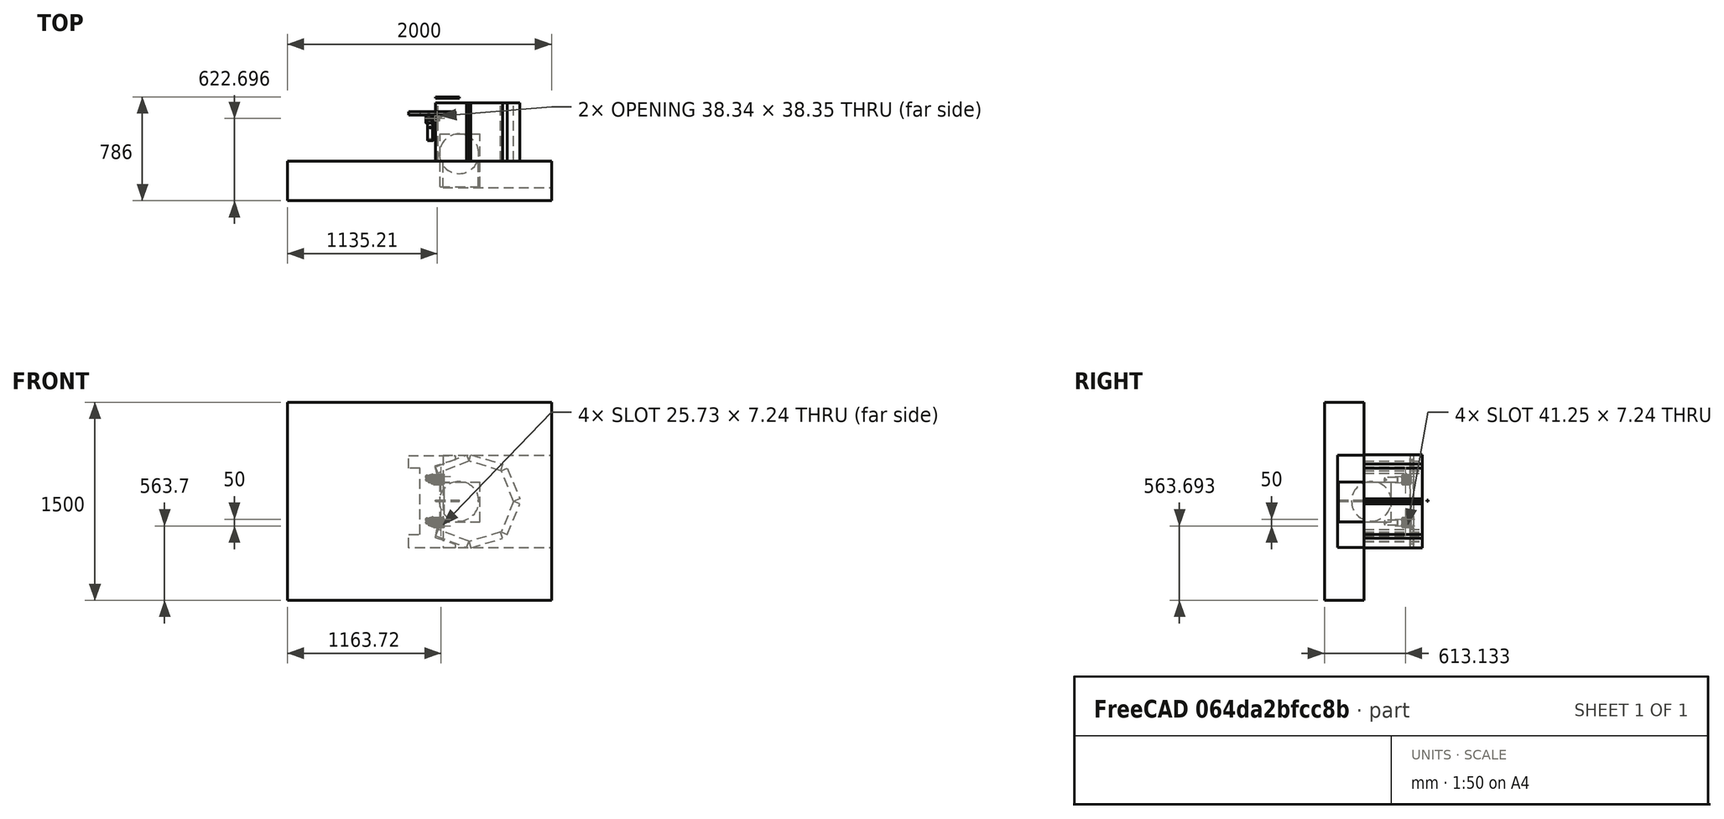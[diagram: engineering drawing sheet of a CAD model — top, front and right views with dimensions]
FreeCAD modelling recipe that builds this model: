
FCSTD DOCUMENT  (FreeCAD 0.17R13541 (Git))
Label: modification4
License: All rights reserved
LicenseURL: http://en.wikipedia.org/wiki/All_rights_reserved
objects: Mesh::Feature×7, Part::Feature×6, Part::Extrusion×6, Part::Box×4, Sketcher::SketchObject×3, Part::Part2DObjectPython×3, Part::Mirroring×3, PartDesign::Pad×2, App::MeasureDistance×2, PartDesign::Body×2, Part::Sphere×1, Part::Cut×1, App::DocumentObjectGroup×1
note: 33 computed .brp shape members not serialized (recipe doc carries the construction recipe); baked Part::Feature solids carry a one-line shape summary decoded from their .brp

FEATURE [Mesh::Feature] main_part  label="main part"
  Placement = pos=(-233.65,190,-253.8) rot=(0,0,1;0rad)
FEATURE [Sketcher::SketchObject] Sketch
  MapMode = 5
  Placement = pos=(0,0,0) rot=(1,0,0;1.5708rad)
  Support = -> [XZ_Plane]
  sketch-geometry (5):
    g0: LineSegment StartX=-1300 StartY=750 StartZ=0 EndX=700 EndY=750 EndZ=0
    g1: LineSegment StartX=700 StartY=750 StartZ=0 EndX=700 EndY=-750 EndZ=0
    g2: LineSegment StartX=700 StartY=-750 StartZ=0 EndX=-1300 EndY=-750 EndZ=0
    g3: LineSegment StartX=-1300 StartY=-750 StartZ=0 EndX=-1300 EndY=750 EndZ=0
    g4: LineSegment [constr] StartX=0 StartY=0 StartZ=0 EndX=700 EndY=0 EndZ=0
  constraints (15):
    c: Coincident(g0,g1)
    c: Coincident(g1,g2)
    c: Coincident(g2,g3)
    c: Coincident(g3,g0)
    c: Horizontal(g0)
    c: Horizontal(g2)
    c: Vertical(g1)
    c: Vertical(g3)
    c: Symmetric(g0,g1,g-1)
    c: DistanceY(g1,g1) = 1500
    c: Distance(g0) = 2000
    c: PointOnObject(g4,g1)
    c: Horizontal(g4)
    c: Coincident(g4,g-1)
    c: DistanceX(g4,g4) = 700
FEATURE [PartDesign::Pad] Pad
  Length = 300
  Length2 = 100
  Placement = pos=(0,0,0) rot=(1,0,0;1.5708rad)
  Profile = -> Sketch
  Type = 0
FEATURE [App::MeasureDistance] Distance  label="Distance: 602.90 mm"
  Distance = 602.898
  P1 = (101.677,440,301.449)
  P2 = (101.677,440,-301.449)
FEATURE [Mesh::Feature] _legs  label="4legs"
  Placement = pos=(-233.65,190,-253.8) rot=(0,0,1;0rad)
FEATURE [Mesh::Feature] _supports  label="4supports"
  Placement = pos=(-233.65,190,-253.8) rot=(0,0,1;0rad)
FEATURE [Mesh::Feature] frame
  Placement = pos=(-233.65,190,-253.8) rot=(0,0,1;0rad)
FEATURE [Mesh::Feature] scanhead
  Placement = pos=(-233.65,190,-253.8) rot=(0,0,1;0rad)
FEATURE [Mesh::Feature] NDD
  Placement = pos=(-233.65,190,-253.8) rot=(0,0,1;0rad)
FEATURE [Mesh::Feature] baseplate
  Placement = pos=(-233.65,190,-253.8) rot=(0,0,1;0rad)
FEATURE [Sketcher::SketchObject] Sketch002
  AttachmentOffset = pos=(0,0,-375) rot=(0,0,1;0rad)
  MapMode = 5
  Placement = pos=(0,375,3.9e-11) rot=(1,0,0;1.5708rad)
  Support = -> [XZ_Plane001]
  sketch-geometry (16):
    g0: LineSegment StartX=-381.934 StartY=346.795 StartZ=0 EndX=-29.0273 EndY=346.795 EndZ=0
    g1: LineSegment StartX=-29.0273 StartY=346.795 StartZ=0 EndX=-29.0273 EndY=314.886 EndZ=0
    g2: LineSegment StartX=-29.0273 StartY=314.886 StartZ=0 EndX=-185.502 EndY=264.81 EndZ=0
    g3: LineSegment StartX=-185.502 StartY=264.81 StartZ=0 EndX=-168.803 EndY=207.974 EndZ=0
    g4: LineSegment StartX=-168.803 StartY=207.974 StartZ=0 EndX=-114.949 EndY=205.162 EndZ=0
    g5: LineSegment StartX=-114.949 StartY=205.162 StartZ=0 EndX=-114.949 EndY=-201.338 EndZ=0
    g6: LineSegment StartX=-114.949 StartY=-201.338 StartZ=0 EndX=-167.27 EndY=-205.799 EndZ=0
    g7: LineSegment StartX=-167.27 StartY=-205.799 StartZ=0 EndX=-182.648 EndY=-273.392 EndZ=0
    g8: LineSegment StartX=-182.648 StartY=-273.392 StartZ=0 EndX=-29.0215 EndY=-323.099 EndZ=0
    g9: LineSegment StartX=-29.0215 StartY=-323.099 StartZ=0 EndX=-29.0215 EndY=-352.213 EndZ=0
    g10: LineSegment StartX=-29.0215 StartY=-352.213 StartZ=0 EndX=-381.23 EndY=-352.213 EndZ=0
    g11: LineSegment StartX=-381.23 StartY=-352.213 StartZ=0 EndX=-381.23 EndY=-251.379 EndZ=0
    g12: LineSegment StartX=-381.23 StartY=-251.379 StartZ=0 EndX=-296.018 EndY=-251.379 EndZ=0
    g13: LineSegment StartX=-296.018 StartY=-251.379 StartZ=0 EndX=-296.018 EndY=249.512 EndZ=0
    g14: LineSegment StartX=-296.018 StartY=249.512 StartZ=0 EndX=-381.934 EndY=249.512 EndZ=0
    g15: LineSegment StartX=-381.934 StartY=249.512 StartZ=0 EndX=-381.934 EndY=346.795 EndZ=0
  constraints (26):
    c: Horizontal(g0)
    c: Coincident(g0,g1)
    c: Vertical(g1)
    c: Coincident(g1,g2)
    c: Coincident(g2,g3)
    c: Coincident(g3,g4)
    c: Coincident(g4,g5)
    c: Vertical(g5)
    c: Coincident(g5,g6)
    c: Coincident(g6,g7)
    c: Coincident(g7,g8)
    c: Coincident(g8,g9)
    c: Vertical(g9)
    c: Coincident(g9,g10)
    c: Horizontal(g10)
    c: Coincident(g10,g11)
    c: Vertical(g11)
    c: Coincident(g11,g12)
    c: Horizontal(g12)
    c: Coincident(g12,g13)
    c: Vertical(g13)
    c: Coincident(g13,g14)
    c: Horizontal(g14)
    c: Coincident(g14,g15)
    c: Vertical(g15)
    c: Coincident(g15,g0)
FEATURE [PartDesign::Pad] Pad002
  Length = 25
  Length2 = 100
  Placement = pos=(0,0,0) rot=(1,0,0;1.5708rad)
  Profile = -> Sketch002
  Type = 0
FEATURE [PartDesign::Body] Body001
  Group = -> [Sketch002,Pad002]
  Origin = -> Origin001
  Tip = -> Pad002
FEATURE [Part::Box] Box  label="Cube"
  AttacherType = Attacher::AttachEngine3D
  Height = 10
  Length = 180
  Placement = pos=(-178,476,0) rot=(0,0,1;0rad)
  Width = 10
FEATURE [Part::Sphere] Sphere
  Angle1 = -90
  Angle2 = 90
  Angle3 = 360
  AttacherType = Attacher::AttachEngine3D
  Placement = pos=(0,55,0) rot=(0,0,1;0rad)
  Radius = 150
FEATURE [Part::Box] Box001  label="Cube001"
  AttacherType = Attacher::AttachEngine3D
  Height = 302
  Length = 302
  Placement = pos=(-144,-194,-156) rot=(0,0,1;0rad)
  Width = 400
FEATURE [Part::Feature] Part__Feature002  label="LPH250-E0W001"
  Placement = pos=(36,41,233) rot=(1,0,0;1.5708rad)
  shape: bbox 76.2 x 274.8 x 98.13 mm, 1972 faces, 0 solids (baked)
FEATURE [Part::Feature] Part__Feature003  label="0701-E0W001"
  Placement = pos=(-219,255,162) rot=(0,0,1;0rad)
  shape: bbox 37.74 x 200 x 37.74 mm, 44 faces (baked)
FEATURE [Part::Feature] Part__Feature006  label="TTN038315-E0W"
  Placement = pos=(-243,310,110) rot=(0,1,0;1.5708rad)
  shape: bbox 136.2 x 63.5 x 82.81 mm, 771 faces, 12 solids (baked)
FEATURE [Part::Feature] Part__Feature007  label="TTN038315-E0W001"
  Placement = pos=(-243,310,-214) rot=(0,1,0;1.5708rad)
  shape: bbox 136.2 x 63.5 x 82.81 mm, 771 faces, 12 solids (baked)
FEATURE [Part::Feature] Part__Feature008  label="LPH250-E0W002"
  Placement = pos=(36,41,-89) rot=(1,0,0;1.5708rad)
  shape: bbox 76.2 x 274.8 x 98.13 mm, 1972 faces, 0 solids (baked)
FEATURE [Part::Feature] Part__Feature009  label="0701-E0W002"
  Placement = pos=(-219,255,-163) rot=(0,0,1;0rad)
  shape: bbox 37.74 x 200 x 37.74 mm, 44 faces (baked)
FEATURE [Part::Box] Box002  label="Cube002"
  AttacherType = Attacher::AttachEngine3D
  Height = 10
  Length = 10
  Placement = pos=(145,-197,0) rot=(0,0,1;0rad)
  Width = 200
FEATURE [Sketcher::SketchObject] Sketch001
  AttachmentOffset = pos=(-20,0,0) rot=(0,0,1;0rad)
  MapMode = 5
  Placement = pos=(-20,0,0) rot=(-1,0,0;1.5708rad)
  Support = -> [Pad]
  sketch-geometry (24):
    g0: LineSegment StartX=-153.123 StartY=262.289 StartZ=0 EndX=81.8002 EndY=347.794 EndZ=0
    g1: LineSegment StartX=81.8002 StartY=347.794 StartZ=0 EndX=98.9012 EndY=300.809 EndZ=0
    g2: LineSegment StartX=98.9012 StartY=300.809 StartZ=0 EndX=-136.022 EndY=215.304 EndZ=0
    g3: LineSegment StartX=-136.022 StartY=215.304 StartZ=0 EndX=-153.123 EndY=262.289 EndZ=0
    g4: LineSegment StartX=118.778 StartY=348.433 StartZ=0 EndX=353.701 EndY=262.928 EndZ=0
    g5: LineSegment StartX=101.677 StartY=301.449 StartZ=0 EndX=118.778 EndY=348.433 EndZ=0
    g6: LineSegment StartX=336.6 StartY=215.944 StartZ=0 EndX=101.677 EndY=301.449 EndZ=0
    g7: LineSegment StartX=353.701 StartY=262.928 StartZ=0 EndX=336.6 EndY=215.944 EndZ=0
    g8: LineSegment StartX=463.416 StartY=0.832942 StartZ=0 EndX=338.416 EndY=217.339 EndZ=0
    g9: LineSegment StartX=381.717 StartY=242.339 StartZ=0 EndX=506.717 EndY=25.8329 EndZ=0
    g10: LineSegment StartX=506.717 StartY=25.8329 StartZ=0 EndX=463.416 EndY=0.832942 EndZ=0
    g11: LineSegment StartX=338.416 StartY=217.339 StartZ=0 EndX=381.717 EndY=242.339 EndZ=0
    g12: LineSegment StartX=-153.123 StartY=-262.289 StartZ=0 EndX=81.8002 EndY=-347.794 EndZ=0
    g13: LineSegment StartX=81.8002 StartY=-347.794 StartZ=0 EndX=98.9012 EndY=-300.809 EndZ=0
    g14: LineSegment StartX=98.9012 StartY=-300.809 StartZ=0 EndX=-136.022 EndY=-215.304 EndZ=0
    g15: LineSegment StartX=-136.022 StartY=-215.304 StartZ=0 EndX=-153.123 EndY=-262.289 EndZ=0
    g16: LineSegment StartX=118.778 StartY=-348.433 StartZ=0 EndX=353.701 EndY=-262.928 EndZ=0
    g17: LineSegment StartX=101.677 StartY=-301.449 StartZ=0 EndX=118.778 EndY=-348.433 EndZ=0
    g18: LineSegment StartX=336.6 StartY=-215.944 StartZ=0 EndX=101.677 EndY=-301.449 EndZ=0
    g19: LineSegment StartX=353.701 StartY=-262.928 StartZ=0 EndX=336.6 EndY=-215.944 EndZ=0
    g20: LineSegment StartX=463.416 StartY=-0.832942 StartZ=0 EndX=338.416 EndY=-217.339 EndZ=0
    g21: LineSegment StartX=381.717 StartY=-242.339 StartZ=0 EndX=506.717 EndY=-25.8329 EndZ=0
    g22: LineSegment StartX=506.717 StartY=-25.8329 StartZ=0 EndX=463.416 EndY=-0.832942 EndZ=0
    g23: LineSegment StartX=338.416 StartY=-217.339 StartZ=0 EndX=381.717 EndY=-242.339 EndZ=0
  constraints (57):
    c: Coincident(g0,g1)
    c: Coincident(g1,g2)
    c: Coincident(g2,g3)
    c: Coincident(g3,g0)
    c: Distance(g0) = 250
    c: Distance(g3) = 50
    c: Equal(g0,g2)
    c: Equal(g3,g1)
    c: Perpendicular(g0,g3)
    c: Coincident(g4,g7)
    c: Coincident(g7,g6)
    c: Coincident(g6,g5)
    c: Coincident(g5,g4)
    c: Equal(g0,g4) = 250
    c: Equal(g3,g5) = 50
    c: Equal(g4,g6)
    c: Equal(g5,g7)
    c: Perpendicular(g4,g5)
    c: Angle(g-1,g2) = 0.349066
    c: Angle(g6,g-1) = 0.349066
    c: Coincident(g9,g10)
    c: Coincident(g10,g8)
    c: Coincident(g8,g11)
    c: Coincident(g11,g9)
    c: Equal(g0,g9) = 250
    c: Equal(g3,g11) = 50
    c: Equal(g9,g8)
    c: Equal(g11,g10)
    c: Perpendicular(g9,g11)
    c: Angle(g8,g-1) = 1.0472
    c: Coincident(g12,g13)
    c: Coincident(g13,g14)
    c: Coincident(g14,g15)
    c: Coincident(g15,g12)
    c: Distance(g12) = 250
    c: Distance(g15) = 50
    c: Equal(g12,g14)
    c: Equal(g15,g13)
    c: Perpendicular(g12,g15)
    c: Coincident(g16,g19)
    c: Coincident(g19,g18)
    c: Coincident(g18,g17)
    c: Coincident(g17,g16)
    c: Equal(g12,g16) = 250
    c: Equal(g15,g17) = 50
    c: Equal(g16,g18)
    c: Equal(g17,g19)
    c: Perpendicular(g16,g17)
    c: Coincident(g21,g22)
    c: Coincident(g22,g20)
    c: Coincident(g20,g23)
    c: Coincident(g23,g21)
    c: Equal(g12,g21) = 250
    c: Equal(g15,g23) = 50
    c: Equal(g21,g20)
    c: Equal(g23,g22)
    c: Perpendicular(g21,g23)
FEATURE [PartDesign::Body] Body
  Group = -> [Sketch,Pad,Sketch001]
  Origin = -> Origin
  Tip = -> Pad
FEATURE [Part::Box] Box003  label="Cube003"
  AttacherType = Attacher::AttachEngine3D
  Height = 700
  Length = 1000
  Placement = pos=(-122,-202,-351) rot=(0,0,1;0rad)
  Width = 800
FEATURE [Part::Cut] Cut
  Base = -> Body
  Tool = -> Box003
FEATURE [App::MeasureDistance] Distance001  label="Distance: 0.82 m"
  Distance = 817.604
  P1 = (-117.595,-2.6e-11,254.633)
  P2 = (700,-2.6e-11,250.791)
FEATURE [Part::Part2DObjectPython] Rectangle  # Draft 2D object (typed FeaturePython)
  ChamferSize = 0
  Columns = 1
  FilletRadius = 0
  Height = 50
  Length = 250
  MakeFace = true
  Placement = pos=(-176.831,0,260.259) rot=(-0.96709,-0.179911,-0.179911;1.60425rad)
  Rows = 1
FEATURE [Part::Part2DObjectPython] Rectangle003  # Draft 2D object (typed FeaturePython)
  ChamferSize = 0
  Columns = 1
  FilletRadius = 0
  Height = 50
  Length = 250
  MakeFace = true
  Placement = pos=(90.1062,0,352.726) rot=(-0.979016,0.144097,0.144097;1.592rad)
  Rows = 1
FEATURE [Part::Part2DObjectPython] Rectangle004  # Draft 2D object (typed FeaturePython)
  ChamferSize = 0
  Columns = 1
  FilletRadius = 0
  Height = 50
  Length = 250
  MakeFace = true
  Placement = pos=(365.777,0,251.4) rot=(-0.723984,0.487774,0.487774;1.88831rad)
  Rows = 1
FEATURE [Part::Mirroring] mirror  label="Mirror of Rectangle"
  Base = (0,0,0)
  Normal = (0,0,1)
  Source = -> Rectangle
FEATURE [Part::Mirroring] mirror001  label="Mirror of Rectangle003"
  Base = (0,0,0)
  Normal = (0,0,1)
  Source = -> Rectangle003
FEATURE [Part::Mirroring] mirror002  label="Mirror of Rectangle004"
  Base = (0,0,0)
  Normal = (0,0,1)
  Source = -> Rectangle004
FEATURE [App::DocumentObjectGroup] Construction
  Group = -> [Rectangle,Rectangle003,Rectangle004,mirror,mirror001,mirror002]
FEATURE [Part::Extrusion] Extrude
  Base = -> Rectangle
  Dir = (0,1,0)
  DirMode = 2
  FaceMakerClass = Part::FaceMakerBullseye
  LengthFwd = 440
  LengthRev = 0
  Solid = false
  Symmetric = false
FEATURE [Part::Extrusion] Extrude001
  Base = -> Rectangle003
  Dir = (0,1,0)
  DirMode = 2
  FaceMakerClass = Part::FaceMakerBullseye
  LengthFwd = 440
  LengthRev = 0
  Solid = false
  Symmetric = false
FEATURE [Part::Extrusion] Extrude002
  Base = -> Rectangle004
  Dir = (0,1,0)
  DirMode = 2
  FaceMakerClass = Part::FaceMakerBullseye
  LengthFwd = 440
  LengthRev = 0
  Solid = false
  Symmetric = false
FEATURE [Part::Extrusion] Extrude003
  Base = -> mirror
  Dir = (0,1,0)
  DirMode = 2
  FaceMakerClass = Part::FaceMakerBullseye
  LengthFwd = 440
  LengthRev = 0
  Solid = false
  Symmetric = false
FEATURE [Part::Extrusion] Extrude004
  Base = -> mirror001
  Dir = (0,1,0)
  DirMode = 2
  FaceMakerClass = Part::FaceMakerBullseye
  LengthFwd = 440
  LengthRev = 0
  Solid = false
  Symmetric = false
FEATURE [Part::Extrusion] Extrude005
  Base = -> mirror002
  Dir = (0,1,0)
  DirMode = 2
  FaceMakerClass = Part::FaceMakerBullseye
  LengthFwd = 440
  LengthRev = 0
  Solid = false
  Symmetric = false
